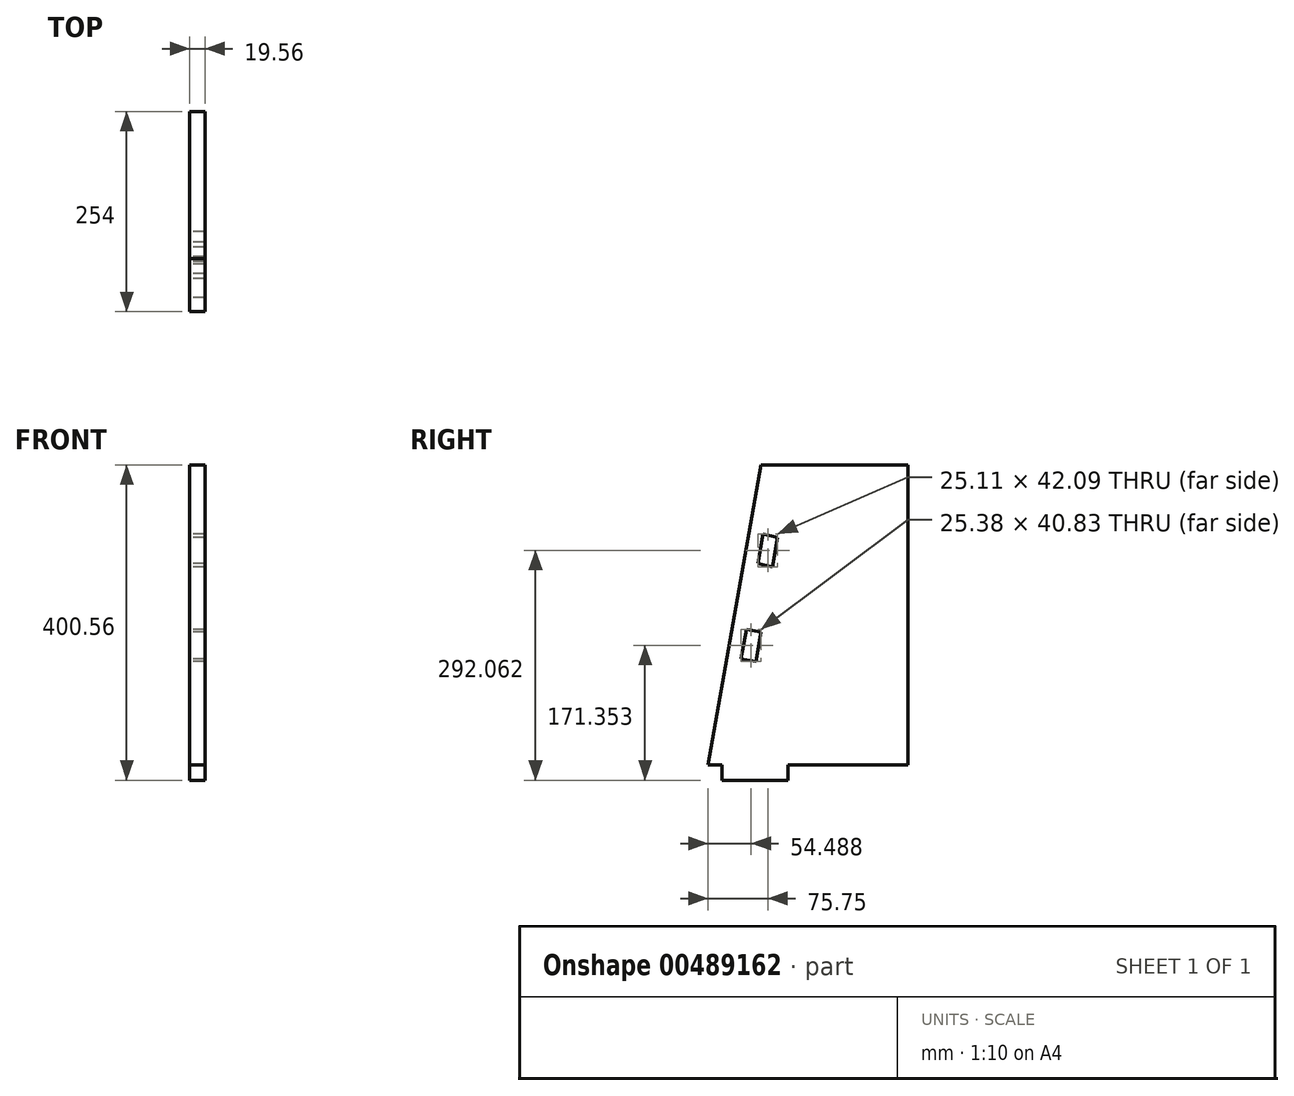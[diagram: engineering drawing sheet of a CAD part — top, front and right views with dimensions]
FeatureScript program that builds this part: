
annotation { "Feature Type Name" : "Feature", "Feature Type Description" : "" }
export const myFeature = defineFeature(function(context is Context, id is Id, definition is map)
    precondition{}
    {
        {
            var Q0;
            Q0=qCreatedBy(makeId("Right.planeOp"),FACE);
            var sketch = newSketch(context, id + "F0", { "sketchPlane" : qUnion([Q0])});
            skLineSegment(sketch, "E0", {"start": v(-85.13, -212.4) * mm, "end": v(-17.95, -212.4) * mm});
            skLineSegment(sketch, "E1", {"start": v(-17.95, 168.6) * mm, "end": v(-85.13, -212.4) * mm});
            skLineSegment(sketch, "E2.bottom", {"start": v(-17.95, 168.6) * mm, "end": v(168.87, 168.6) * mm});
            skLineSegment(sketch, "E2.top", {"start": v(-17.95, -212.4) * mm, "end": v(168.87, -212.4) * mm});
            skLineSegment(sketch, "E2.right", {"start": v(168.87, 168.6) * mm, "end": v(168.87, -212.4) * mm});
            skLineSegment(sketch, "E3.bottom", {"start": v(-67.35, -212.4) * mm, "end": v(16.47, -212.4) * mm});
            skLineSegment(sketch, "E3.top", {"start": v(-67.35, -231.95) * mm, "end": v(16.47, -231.95) * mm});
            skLineSegment(sketch, "E3.left", {"start": v(-67.35, -212.4) * mm, "end": v(-67.35, -231.95) * mm});
            skLineSegment(sketch, "E3.right", {"start": v(16.47, -212.4) * mm, "end": v(16.47, -231.95) * mm});
            skLineSegment(sketch, "E4.bottom", {"start": v(67.27, -212.4) * mm, "end": v(151.09, -212.4) * mm});
            skLineSegment(sketch, "E4.top", {"start": v(67.27, -231.95) * mm, "end": v(151.09, -231.95) * mm});
            skLineSegment(sketch, "E4.left", {"start": v(67.27, -212.4) * mm, "end": v(67.27, -231.95) * mm});
            skLineSegment(sketch, "E4.right", {"start": v(151.09, -212.4) * mm, "end": v(151.09, -231.95) * mm});
            skLineSegment(sketch, "E5", {"start": v(-43.33, -77.7) * mm, "end": v(-24.57, -81.01) * mm});
            skLineSegment(sketch, "E6", {"start": v(-43.33, -77.7) * mm, "end": v(-36.71, -40.18) * mm});
            skLineSegment(sketch, "E7", {"start": v(-36.71, -40.18) * mm, "end": v(-17.95, -43.49) * mm});
            skLineSegment(sketch, "E8", {"start": v(-24.57, -81.01) * mm, "end": v(-17.95, -43.49) * mm});
            skPoint(sketch, "E9.startSnap0", {"position": v(-27.33, -41.84) * mm});
            skLineSegment(sketch, "E10", {"start": v(-21.93, 43.64) * mm, "end": v(-15.32, 81.16) * mm});
            skLineSegment(sketch, "E11", {"start": v(-15.32, 81.16) * mm, "end": v(3.17, 76.59) * mm});
            skLineSegment(sketch, "E12", {"start": v(3.17, 76.59) * mm, "end": v(-3.44, 39.06) * mm});
            skLineSegment(sketch, "E13", {"start": v(-3.44, 39.06) * mm, "end": v(-17.95, 42.65) * mm});
            skLineSegment(sketch, "E14", {"start": v(-17.95, 42.65) * mm, "end": v(-21.93, 43.64) * mm});
            skSolve(sketch);
        }
        {
            var Q0;
            {var subQ0=sQuery(id+"F0.wireOp",EDGE,"E0");Q0=makeQuery(id+"F0.imprint","IMPRINT",FACE,{"disambiguationData":[TD([[makeQuery(id+"F0.imprint","IMPRINT",EDGE,{"derivedFrom":subQ0}),1.0]])]});}
            var Q1;
            Q1=makeQuery(id+"F0.imprint","IMPRINT",FACE,{"disambiguationData":[TD([[makeQuery(id+"F0.imprint","IMPRINT",EDGE,{"derivedFrom":sQuery(id+"F0.wireOp",EDGE,"E2.bottom")}),-1.0]])]});
            var Q2;
            Q2=makeQuery(id+"F0.imprint","IMPRINT",FACE,{"disambiguationData":[TD([[makeQuery(id+"F0.imprint","IMPRINT",EDGE,{"derivedFrom":sQuery(id+"F0.wireOp",EDGE,"E3.top")}),1.0]])]});
            var Q3;
            Q3=makeQuery(id+"F0.imprint","IMPRINT",FACE,{"disambiguationData":[TD([[makeQuery(id+"F0.imprint","IMPRINT",EDGE,{"derivedFrom":sQuery(id+"F0.wireOp",EDGE,"E4.bottom")}),-1.0]])]});
            extrude(context, id + "F1", {"entities" : qUnion([Q0, Q1, Q2, Q3]), "depth" : 19.56 * mm, "offsetDistance" : 25.4 * mm});
        }
    });
